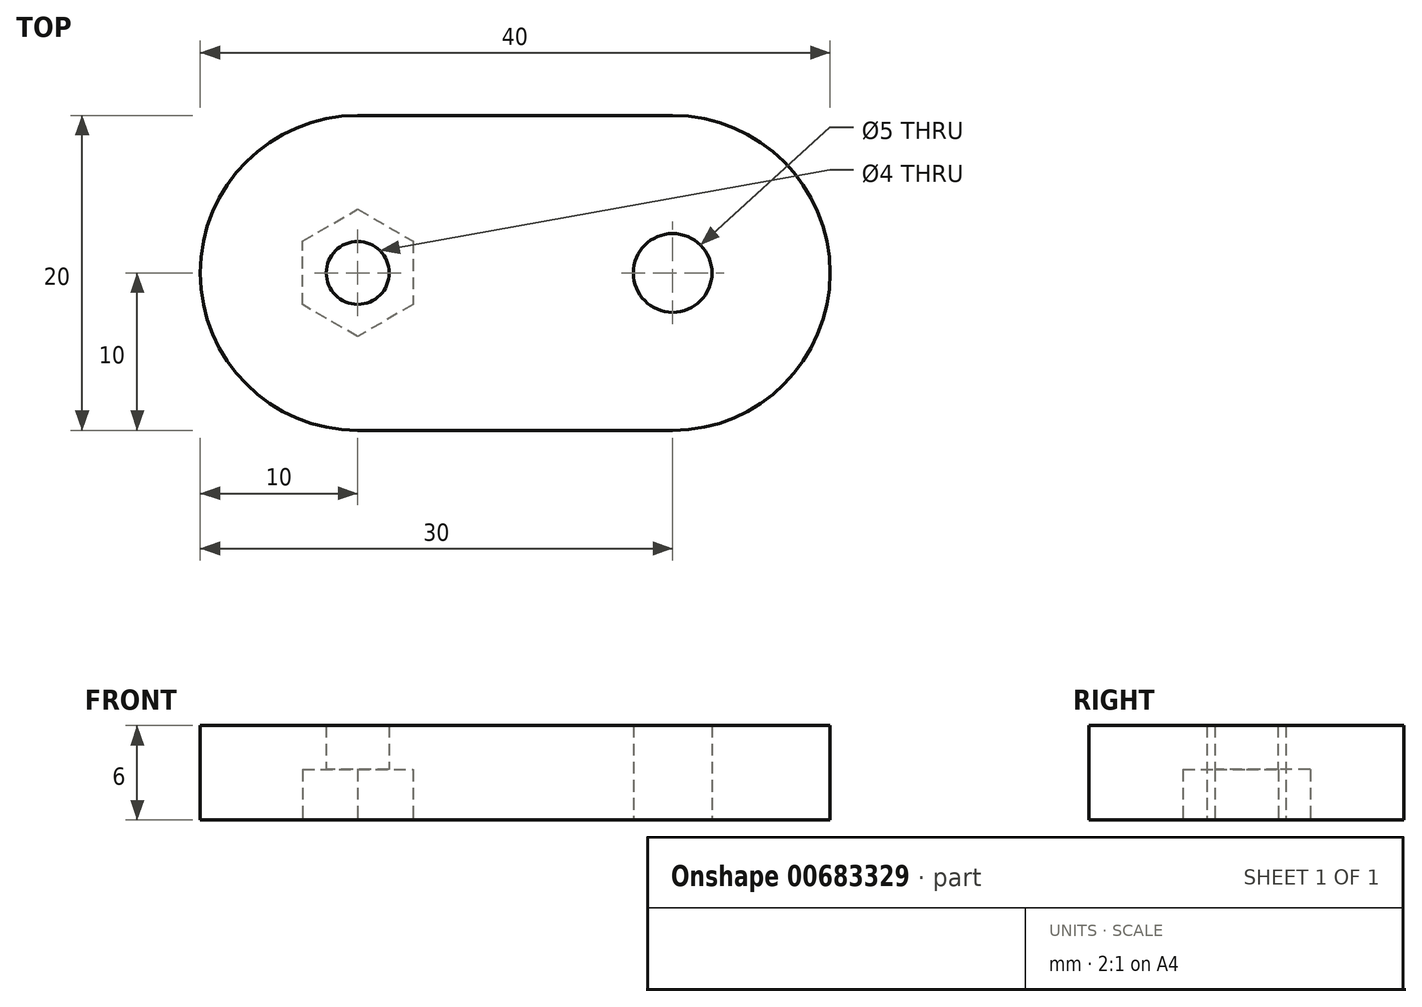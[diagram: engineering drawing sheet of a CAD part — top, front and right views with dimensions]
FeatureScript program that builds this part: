
annotation { "Feature Type Name" : "Feature", "Feature Type Description" : "" }
export const myFeature = defineFeature(function(context is Context, id is Id, definition is map)
    precondition{}
    {
        {
            var Q0;
            Q0=qCreatedBy(makeId("Top.planeOp"),FACE);
            var sketch = newSketch(context, id + "F0", { "sketchPlane" : qUnion([Q0])});
            skLineSegment(sketch, "E0.bottom", {"start": v(20, 10) * mm, "end": v(-20, 10) * mm});
            skLineSegment(sketch, "E0.top", {"start": v(20, -10) * mm, "end": v(-20, -10) * mm});
            skLineSegment(sketch, "E0.left", {"start": v(20, 10) * mm, "end": v(20, -10) * mm});
            skLineSegment(sketch, "E0.right", {"start": v(-20, 10) * mm, "end": v(-20, -10) * mm});
            skPoint(sketch, "E0.middle", {"position": v(0, 0) * mm});
            skLineSegment(sketch, "E1", {"start": v(20, -10) * mm, "end": v(0, -10) * mm});
            skLineSegment(sketch, "E2", {"start": v(0, -10) * mm, "end": v(0, 10) * mm, "construction": true});
            skLineSegment(sketch, "E3", {"start": v(0, 10) * mm, "end": v(20, 10) * mm});
            skLineSegment(sketch, "E4", {"start": v(10, 10) * mm, "end": v(10, -10) * mm, "construction": true});
            skLineSegment(sketch, "E5", {"start": v(0, -10) * mm, "end": v(-20, -10) * mm});
            skLineSegment(sketch, "E6", {"start": v(-10, -10) * mm, "end": v(-10, 10) * mm, "construction": true});
            skCircle(sketch, "E7", {"center": v(-10, 0) * mm, "radius": 2 * mm});
            skCircle(sketch, "E8", {"center": v(10, 0) * mm, "radius": 2.5 * mm});
            skCircle(sketch, "E9.cCircle", {"center": v(-10, 0) * mm, "radius": 3.5 * mm, "construction": true});
            skLineSegment(sketch, "E9.0", {"start": v(-6.5, 2.02) * mm, "end": v(-6.5, -2.02) * mm});
            skLineSegment(sketch, "E9.1", {"start": v(-6.5, -2.02) * mm, "end": v(-10, -4.04) * mm});
            skLineSegment(sketch, "E9.2", {"start": v(-10, -4.04) * mm, "end": v(-13.5, -2.02) * mm});
            skLineSegment(sketch, "E9.3", {"start": v(-13.5, -2.02) * mm, "end": v(-13.5, 2.02) * mm});
            skLineSegment(sketch, "E9.4", {"start": v(-13.5, 2.02) * mm, "end": v(-10, 4.04) * mm});
            skLineSegment(sketch, "E9.5", {"start": v(-10, 4.04) * mm, "end": v(-6.5, 2.02) * mm});
            skPoint(sketch, "E9.0.midPoint", {"position": v(-6.5, 0) * mm});
            skCircle(sketch, "E10", {"center": v(10, 0) * mm, "radius": 5 * mm, "construction": true});
            skSolve(sketch);
        }
        {
            var Q0;
            Q0 = qSketchRegion(id + "F0", true);
            var Q1;
            Q1=makeQuery(id+"F0.imprint","IMPRINT",FACE,{"disambiguationData":[TD([[makeQuery(id+"F0.imprint","IMPRINT",EDGE,{"derivedFrom":sQuery(id+"F0.wireOp",EDGE,"E7")}),-1.0]])]});
            extrude(context, id + "F1", {"entities" : qUnion([Q0, Q1]), "depth" : 6 * mm, "offsetDistance" : 25 * mm});
        }
        {
            var Q0;
            Q0=makeQuery(id+"F0.imprint","IMPRINT",FACE,{"disambiguationData":[TD([[makeQuery(id+"F0.imprint","IMPRINT",EDGE,{"derivedFrom":sQuery(id+"F0.wireOp",EDGE,"E7")}),-1.0]])]});
            extrude(context, id + "F2", {"entities" : qUnion([Q0]), "operationType" : NewBodyOperationType.REMOVE, "depth" : 3.2 * mm, "offsetDistance" : 25 * mm});
        }
        {
            var Q0;
            Q0=makeQuery(id+"F1.opExtrude","SWEPT_EDGE",EDGE,{"disambiguationData":[OSD([sQuery(id+"F0.wireOp",EDGE,"E0.right"),sQuery(id+"F0.wireOp",EDGE,"E5")])]});
            var Q1;
            Q1=makeQuery(id+"F1.opExtrude","SWEPT_EDGE",EDGE,{"disambiguationData":[OSD([sQuery(id+"F0.wireOp",EDGE,"E0.left"),sQuery(id+"F0.wireOp",EDGE,"E1")])]});
            var Q2;
            Q2=makeQuery(id+"F1.opExtrude","SWEPT_EDGE",EDGE,{"disambiguationData":[OSD([sQuery(id+"F0.wireOp",EDGE,"E0.left"),sQuery(id+"F0.wireOp",EDGE,"E3")])]});
            var Q3;
            Q3=makeQuery(id+"F1.opExtrude","SWEPT_EDGE",EDGE,{"disambiguationData":[OSD([sQuery(id+"F0.wireOp",EDGE,"E0.bottom"),sQuery(id+"F0.wireOp",EDGE,"E0.right")])]});
            fillet(context, id + "F3", {"entities" : qUnion([Q0, Q1, Q2, Q3]), "radius" : 10 * mm, "tangentPropagation" : true, "allowEdgeOverflow" : false});
        }
    });
